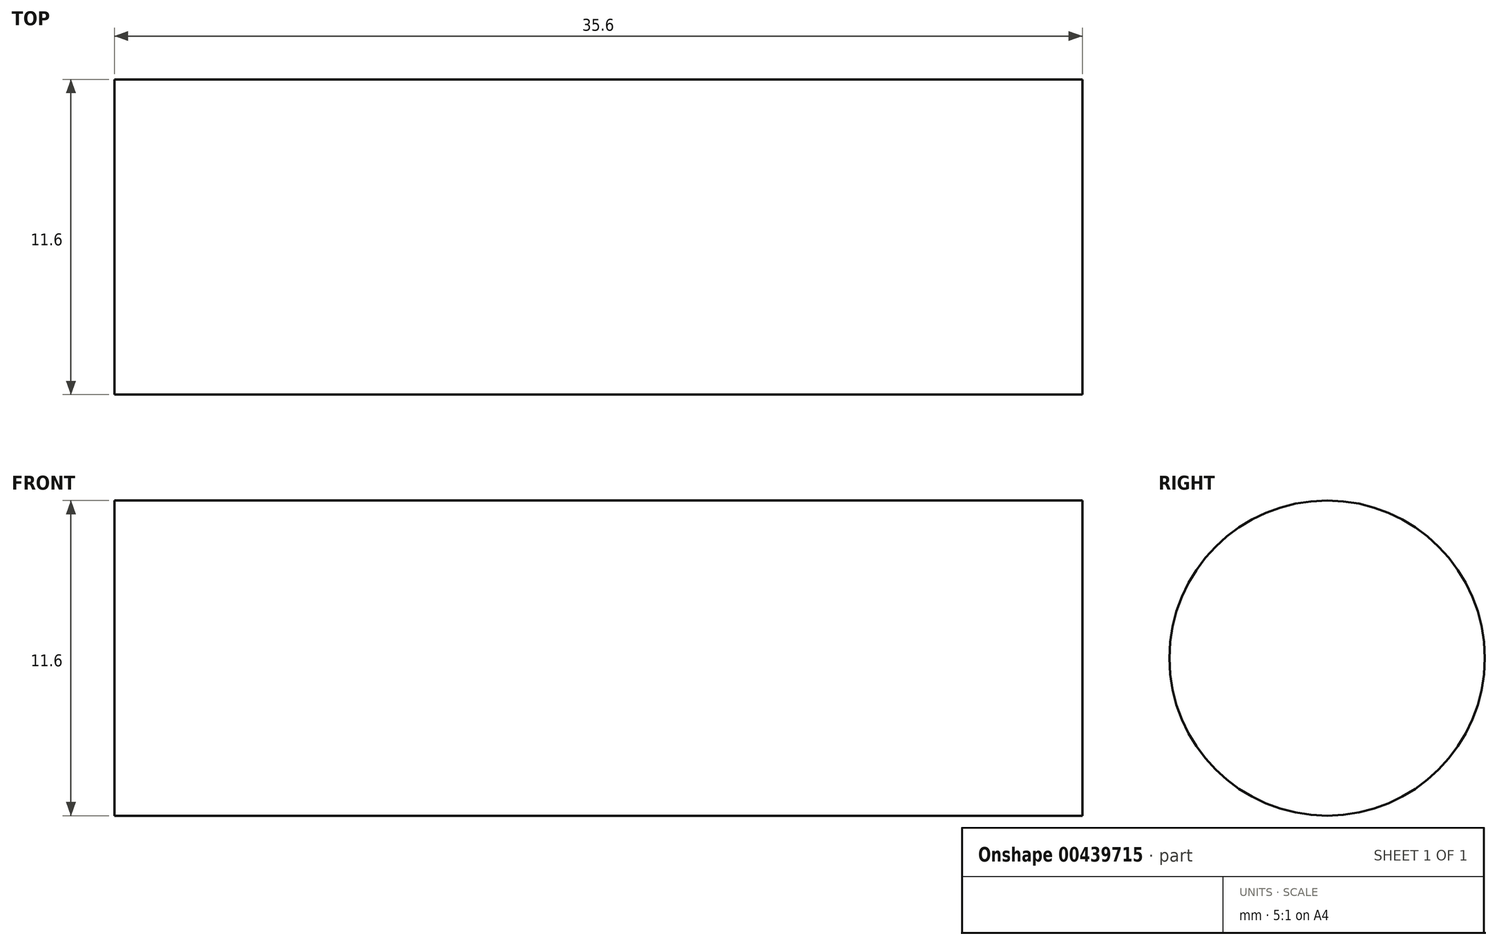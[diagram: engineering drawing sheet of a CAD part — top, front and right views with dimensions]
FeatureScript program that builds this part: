
annotation { "Feature Type Name" : "Feature", "Feature Type Description" : "" }
export const myFeature = defineFeature(function(context is Context, id is Id, definition is map)
    precondition{}
    {
        {
            var Q0;
            Q0=qCreatedBy(makeId("Top.planeOp"),FACE);
            var sketch = newSketch(context, id + "F0", { "sketchPlane" : qUnion([Q0])});
            skLineSegment(sketch, "E0.bottom", {"start": v(-16.78, 0) * mm, "end": v(18.82, 0) * mm});
            skLineSegment(sketch, "E0.top", {"start": v(-16.78, 5.8) * mm, "end": v(18.82, 5.8) * mm});
            skLineSegment(sketch, "E0.left", {"start": v(-16.78, 0) * mm, "end": v(-16.78, 5.8) * mm});
            skLineSegment(sketch, "E0.right", {"start": v(18.82, 0) * mm, "end": v(18.82, 5.8) * mm});
            skLineSegment(sketch, "E1.bottom", {"start": v(15.82, 5.8) * mm, "end": v(13.32, 5.8) * mm});
            skLineSegment(sketch, "E1.top", {"start": v(15.82, 7.8) * mm, "end": v(13.32, 7.8) * mm});
            skLineSegment(sketch, "E1.left", {"start": v(15.82, 5.8) * mm, "end": v(15.82, 7.8) * mm});
            skLineSegment(sketch, "E1.right", {"start": v(13.32, 5.8) * mm, "end": v(13.32, 7.8) * mm});
            skFitSpline(sketch, "E2", {"points": [v(13.32, 5.8) * mm, v(15.82, 7.8) * mm], "startDerivative": vector(1.91, 0) * mm, "endDerivative": vector(4.7, 0) * mm});
            skSolve(sketch);
        }
        {
            var Q0;
            Q0=makeQuery(id+"F0.imprint","IMPRINT",FACE,{"disambiguationData":[TD([[makeQuery(id+"F0.imprint","IMPRINT",EDGE,{"derivedFrom":sQuery(id+"F0.wireOp",EDGE,"E0.bottom")}),1.0]])]});
            var Q1;
            Q1=makeQuery(id+"F0.imprint","IMPRINT",FACE,{"disambiguationData":[TD([[makeQuery(id+"F0.imprint","IMPRINT",EDGE,{"derivedFrom":sQuery(id+"F0.wireOp",EDGE,"E1.bottom")}),-1.0]])]});
            var Q2;
            Q2=sQuery(id+"F0.wireOp",EDGE,"E0.bottom");
            revolve(context, id + "F1", {"entities" : qUnion([Q0, Q1]), "axis" : qUnion([Q2]), "revolveType" : RevolveType.FULL});
        }
    });
